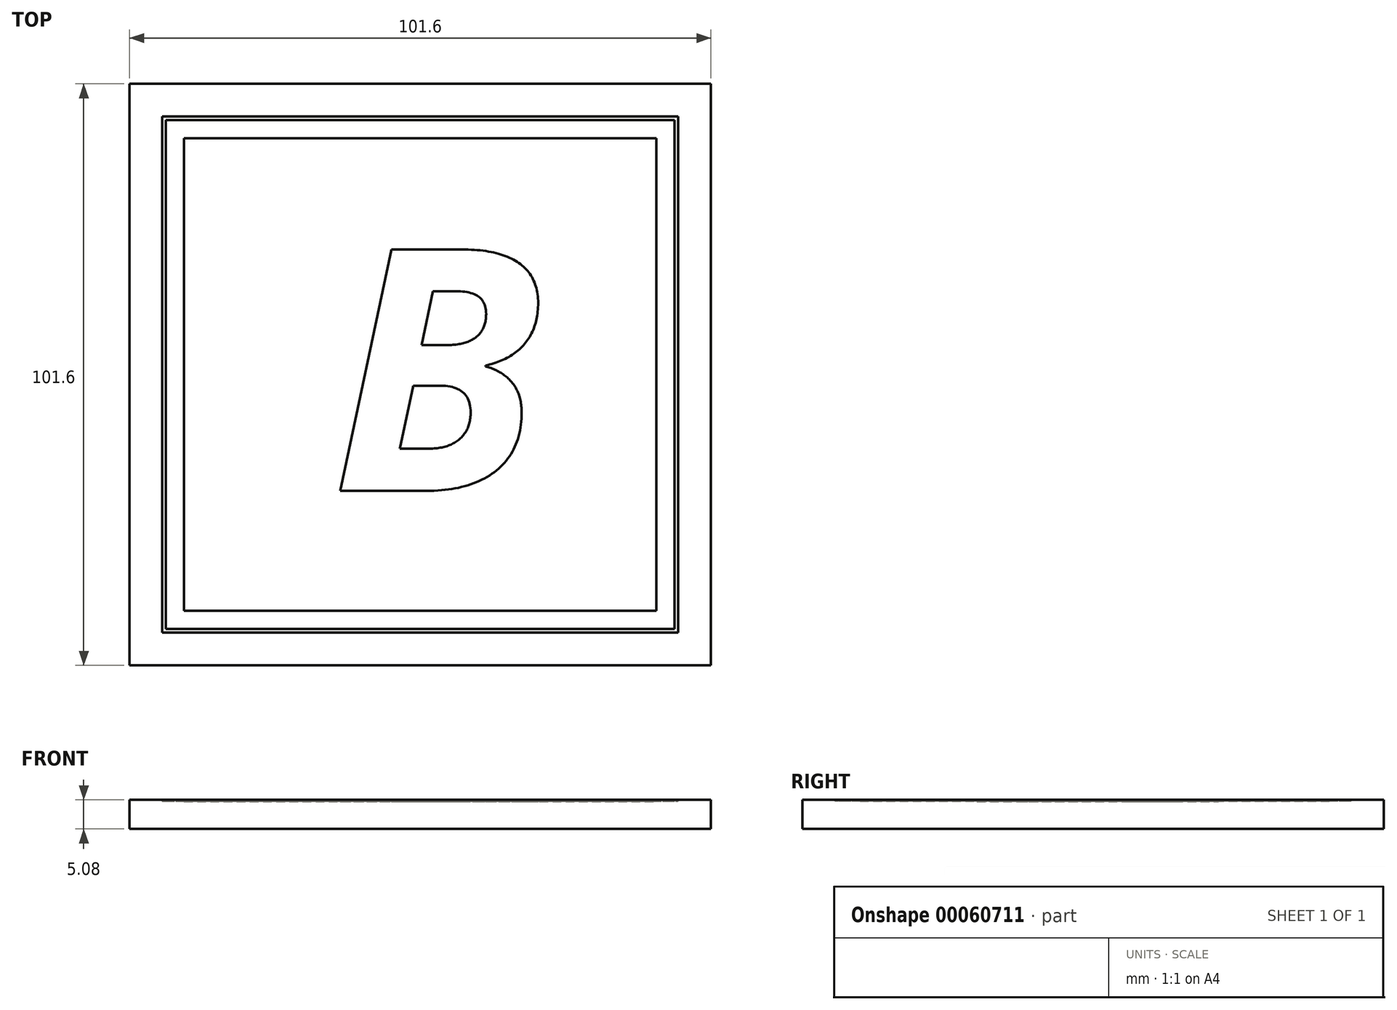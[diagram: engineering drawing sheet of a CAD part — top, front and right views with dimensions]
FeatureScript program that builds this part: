
annotation { "Feature Type Name" : "Feature", "Feature Type Description" : "" }
export const myFeature = defineFeature(function(context is Context, id is Id, definition is map)
    precondition{}
    {
        {
            var Q0;
            Q0=qCreatedBy(makeId("Top.planeOp"),FACE);
            var sketch = newSketch(context, id + "F0", { "sketchPlane" : qUnion([Q0])});
            skLineSegment(sketch, "E0.bottom", {"start": v(-73.78, 50.56) * mm, "end": v(27.82, 50.56) * mm});
            skLineSegment(sketch, "E0.top", {"start": v(-73.78, -51.04) * mm, "end": v(27.82, -51.04) * mm});
            skLineSegment(sketch, "E0.left", {"start": v(-73.78, 50.56) * mm, "end": v(-73.78, -51.04) * mm});
            skLineSegment(sketch, "E0.right", {"start": v(27.82, 50.56) * mm, "end": v(27.82, -51.04) * mm});
            skSolve(sketch);
        }
        {
            var Q0;
            Q0=makeQuery(id+"F0.imprint","IMPRINT",FACE,{"disambiguationData":[TD([[makeQuery(id+"F0.imprint","IMPRINT",EDGE,{"derivedFrom":sQuery(id+"F0.wireOp",EDGE,"E0.bottom")}),-1.0]])]});
            extrude(context, id + "F1", {"entities" : qUnion([Q0]), "depth" : 5.08 * mm});
        }
        {
            var Q0;
            Q0=makeQuery(id+"F1.opExtrude","CAP_FACE",FACE,{"disambiguationData":[OSD([sQuery(id+"F0.wireOp",EDGE,"E0.bottom"),sQuery(id+"F0.wireOp",EDGE,"E0.top"),sQuery(id+"F0.wireOp",EDGE,"E0.left"),sQuery(id+"F0.wireOp",EDGE,"E0.right")])],"isStart":false});
            var sketch = newSketch(context, id + "F2", { "sketchPlane" : qUnion([Q0])});
            skLineSegment(sketch, "E1.bottom", {"start": v(-67.43, 44.21) * mm, "end": v(21.47, 44.21) * mm});
            skLineSegment(sketch, "E1.top", {"start": v(-67.43, -44.69) * mm, "end": v(21.47, -44.69) * mm});
            skLineSegment(sketch, "E1.left", {"start": v(-67.43, 44.21) * mm, "end": v(-67.43, -44.69) * mm});
            skLineSegment(sketch, "E1.right", {"start": v(21.47, 44.21) * mm, "end": v(21.47, -44.69) * mm});
            skLineSegment(sketch, "E2.0", {"start": v(-68.06, 44.85) * mm, "end": v(22.1, 44.85) * mm});
            skLineSegment(sketch, "E2.1", {"start": v(-68.06, 44.85) * mm, "end": v(-68.06, -45.32) * mm});
            skLineSegment(sketch, "E2.2", {"start": v(-68.06, -45.32) * mm, "end": v(22.1, -45.32) * mm});
            skLineSegment(sketch, "E2.3", {"start": v(22.1, 44.85) * mm, "end": v(22.1, -45.32) * mm});
            skSolve(sketch);
        }
        {
            var Q0;
            Q0=makeQuery(id+"F2.imprint","IMPRINT",FACE,{"disambiguationData":[TD([[makeQuery(id+"F2.imprint","IMPRINT",EDGE,{"derivedFrom":sQuery(id+"F2.wireOp",EDGE,"E1.bottom")}),1.0]])]});
            extrude(context, id + "F3", {"entities" : qUnion([Q0]), "operationType" : NewBodyOperationType.REMOVE, "oppositeDirection" : true, "depth" : 0.25 * mm});
        }
        {
            var Q0;
            Q0=makeQuery(id+"F3.boolean.opBoolean","SPLIT",FACE,{"disambiguationData":[TD([makeQuery(id+"F3.opExtrude","SWEPT_FACE",FACE,{"disambiguationData":[OSD([sQuery(id+"F2.wireOp",EDGE,"E1.bottom")])]})])],"derivedFrom":makeQuery(id+"F1.opExtrude","CAP_FACE",FACE,{"disambiguationData":[OSD([sQuery(id+"F0.wireOp",EDGE,"E0.bottom"),sQuery(id+"F0.wireOp",EDGE,"E0.top"),sQuery(id+"F0.wireOp",EDGE,"E0.left"),sQuery(id+"F0.wireOp",EDGE,"E0.right")])],"isStart":false})});
            var sketch = newSketch(context, id + "F4", { "sketchPlane" : qUnion([Q0])});
            skLineSegment(sketch, "E3.0", {"start": v(-64.25, 41.04) * mm, "end": v(18.3, 41.04) * mm});
            skLineSegment(sketch, "E3.1", {"start": v(-64.25, 41.04) * mm, "end": v(-64.25, -41.51) * mm});
            skLineSegment(sketch, "E3.2", {"start": v(-64.25, -41.51) * mm, "end": v(18.3, -41.51) * mm});
            skLineSegment(sketch, "E3.3", {"start": v(18.3, 41.04) * mm, "end": v(18.3, -41.51) * mm});
            skSolve(sketch);
        }
        {
            var Q0;
            Q0 = qSketchRegion(id + "F4", true);
            extrude(context, id + "F5", {"entities" : qUnion([Q0]), "operationType" : NewBodyOperationType.REMOVE, "oppositeDirection" : true, "depth" : 0.32 * mm});
        }
        {
            var Q0;
            Q0=makeQuery(id+"F5.boolean.opBoolean","COPY",FACE,{"derivedFrom":makeQuery(id+"F5.opExtrude","CAP_FACE",FACE,{"disambiguationData":[OSD([sQuery(id+"F4.wireOp",EDGE,"E3.0"),sQuery(id+"F4.wireOp",EDGE,"E3.1"),sQuery(id+"F4.wireOp",EDGE,"E3.2"),sQuery(id+"F4.wireOp",EDGE,"E3.3")])],"isStart":false})});
            var sketch = newSketch(context, id + "F6", { "sketchPlane" : qUnion([Q0])});
            skText(sketch, "E4", { "text": "B", "fontName": "OpenSans-BoldItalic.ttf"});
            const initialGuessF6  = {"E4": [-0.03847, -0.02055, 1, 0, 0.04254]};
            skSetInitialGuess(sketch, initialGuessF6);
            skSolve(sketch);
        }
        {
            var Q0;
            Q0=makeQuery(id+"F6.imprint","IMPRINT",FACE,{"disambiguationData":[TD([[makeQuery(id+"F6.imprint","IMPRINT",EDGE,{"derivedFrom":sQuery(id+"F6.wireOp",EDGE,"E4.sketch_text.stroke-0")}),-1.0]])]});
            var Q1;
            {var subQ0=sQuery(id+"F0.wireOp",EDGE,"E0.right");var subQ1=sQuery(id+"F0.wireOp",EDGE,"E0.left");var subQ2=sQuery(id+"F0.wireOp",EDGE,"E0.top");var subQ3=sQuery(id+"F0.wireOp",EDGE,"E0.bottom");Q1=makeQuery(id+"F3.boolean.opBoolean","SPLIT",FACE,{"disambiguationData":[TD([makeQuery(id+"F1.opExtrude","SWEPT_FACE",FACE,{"disambiguationData":[OSD([subQ3])]})])],"derivedFrom":makeQuery(id+"F1.opExtrude","CAP_FACE",FACE,{"disambiguationData":[OSD([subQ3,subQ2,subQ1,subQ0])],"isStart":false})});}
            extrude(context, id + "F7", {"entities" : qUnion([Q0]), "operationType" : NewBodyOperationType.ADD, "endBound" : BoundingType.UP_TO_SURFACE, "endBoundEntityFace" : qUnion([Q1]), "depth" : 25.4 * mm});
        }
    });
